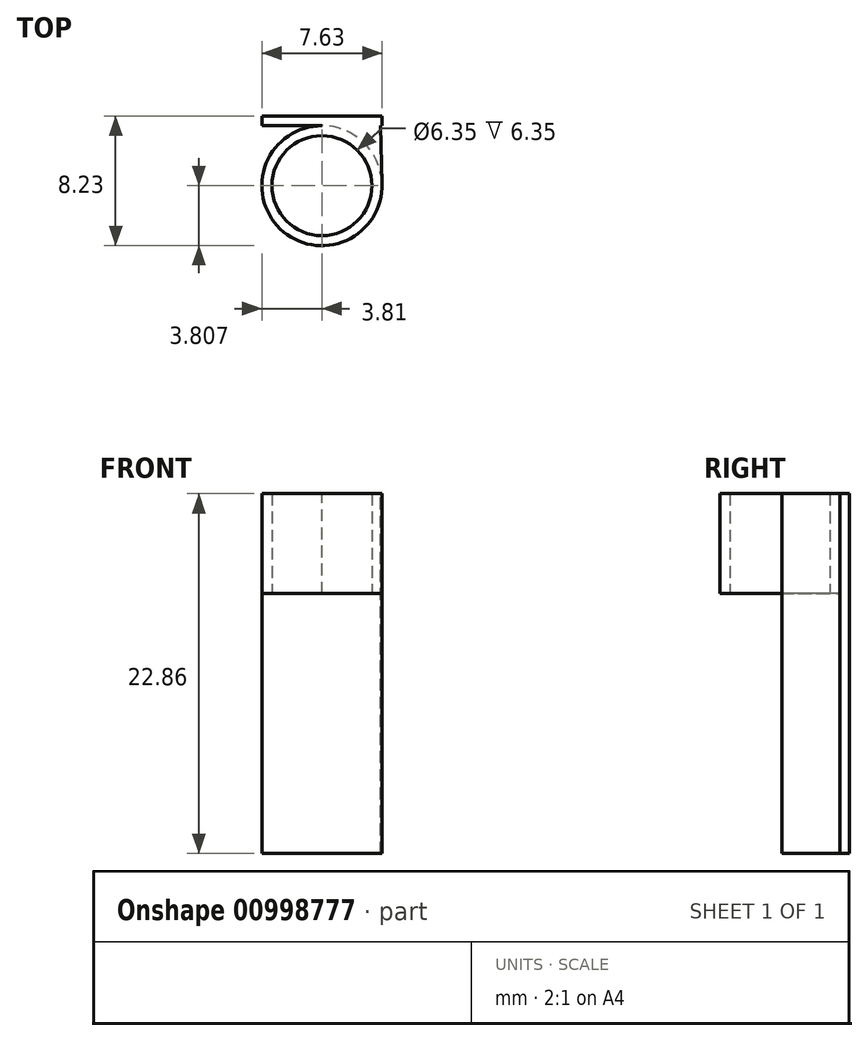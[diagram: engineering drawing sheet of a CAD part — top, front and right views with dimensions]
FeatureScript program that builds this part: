
annotation { "Feature Type Name" : "Feature", "Feature Type Description" : "" }
export const myFeature = defineFeature(function(context is Context, id is Id, definition is map)
    precondition{}
    {
        {
            var Q0;
            Q0=qCreatedBy(makeId("Top.planeOp"),FACE);
            var sketch = newSketch(context, id + "F0", { "sketchPlane" : qUnion([Q0])});
            skCircle(sketch, "E0", {"center": v(0, -1.38) * mm, "radius": 3.18 * mm});
            skCircle(sketch, "E1", {"center": v(0, -1.38) * mm, "radius": 3.81 * mm});
            skSolve(sketch);
        }
        {
            var Q0;
            Q0=makeQuery(id+"F0.imprint","IMPRINT",FACE,{"disambiguationData":[TD([[makeQuery(id+"F0.imprint","IMPRINT",EDGE,{"derivedFrom":sQuery(id+"F0.wireOp",EDGE,"E0")}),-1.0]])]});
            extrude(context, id + "F1", {"entities" : qUnion([Q0]), "depth" : 6.35 * mm, "offsetDistance" : 25.4 * mm});
        }
        {
            var Q0;
            Q0=makeQuery(id+"F1.opExtrude","CAP_FACE",FACE,{"disambiguationData":[OSD([sQuery(id+"F0.wireOp",EDGE,"E0"),sQuery(id+"F0.wireOp",EDGE,"E1")])],"isStart":false});
            var sketch = newSketch(context, id + "F2", { "sketchPlane" : qUnion([Q0])});
            skLineSegment(sketch, "E2", {"start": v(0, -1.38) * mm, "end": v(-3.81, -1.38) * mm});
            skLineSegment(sketch, "E3", {"start": v(-3.81, -1.38) * mm, "end": v(3.81, -1.38) * mm});
            skLineSegment(sketch, "E4", {"start": v(3.81, -1.38) * mm, "end": v(0, -1.38) * mm});
            skLineSegment(sketch, "E5", {"start": v(0, -1.38) * mm, "end": v(0, 2.43) * mm});
            skLineSegment(sketch, "E6", {"start": v(0, 2.43) * mm, "end": v(-6.07, 2.43) * mm});
            skLineSegment(sketch, "E7", {"start": v(-6.07, 2.43) * mm, "end": v(6.94, 2.43) * mm});
            skLineSegment(sketch, "E8", {"start": v(-3.81, -1.38) * mm, "end": v(-3.81, 2.43) * mm});
            skLineSegment(sketch, "E9", {"start": v(-3.81, 2.43) * mm, "end": v(3.74, 2.43) * mm});
            skLineSegment(sketch, "E10", {"start": v(3.81, -1.38) * mm, "end": v(3.74, 2.43) * mm});
            skLineSegment(sketch, "E11.bottom", {"start": v(-3.81, -1.38) * mm, "end": v(3.82, -1.38) * mm});
            skLineSegment(sketch, "E11.top", {"start": v(-3.81, 3.04) * mm, "end": v(3.82, 3.04) * mm});
            skLineSegment(sketch, "E11.left", {"start": v(-3.81, -1.38) * mm, "end": v(-3.81, 3.04) * mm});
            skLineSegment(sketch, "E11.right", {"start": v(3.82, -1.38) * mm, "end": v(3.82, 3.04) * mm});
            skSolve(sketch);
        }
        {
            var Q0;
            {var subQ0=sQuery(id+"F2.wireOp",EDGE,"E9");var subQ3=sQuery(id+"F2.wireOp",EDGE,"E11.left");var subQ4=makeQuery(id+"F2.imprint","INTERSECT",VERTEX,{"derivedFrom":[subQ0,subQ3]});Q0=makeQuery(id+"F2.imprint","IMPRINT",FACE,{"disambiguationData":[TD([[makeQuery(id+"F2.imprint","IMPRINT",EDGE,{"disambiguationData":[TD([[subQ4,-1.0]])],"derivedFrom":subQ0}),-1.0]])]});}
            var Q1;
            {var subQ6=sQuery(id+"F2.wireOp",EDGE,"E11.top");Q1=makeQuery(id+"F2.imprint","IMPRINT",FACE,{"disambiguationData":[TD([[makeQuery(id+"F2.imprint","IMPRINT",EDGE,{"derivedFrom":subQ6}),-1.0]])]});}
            var Q2;
            {var subQ1=makeQuery(id+"F1.opExtrude","CAP_EDGE",EDGE,{"disambiguationData":[OSD([sQuery(id+"F0.wireOp",EDGE,"E1")])],"isStart":false});var subQ3=sQuery(id+"F2.wireOp",EDGE,"E10");var subQ5=makeQuery(id+"F2.imprint","INTERSECT",VERTEX,{"derivedFrom":[subQ1,subQ3]});Q2=makeQuery(id+"F2.imprint","IMPRINT",FACE,{"disambiguationData":[TD([[makeQuery(id+"F2.imprint","IMPRINT",EDGE,{"disambiguationData":[TD([[subQ5,-1.0]])],"derivedFrom":subQ3}),1.0]])]});}
            extrude(context, id + "F3", {"entities" : qUnion([Q0, Q1, Q2]), "operationType" : NewBodyOperationType.ADD, "oppositeDirection" : true, "depth" : 22.86 * mm, "offsetDistance" : 25.4 * mm});
        }
    });
